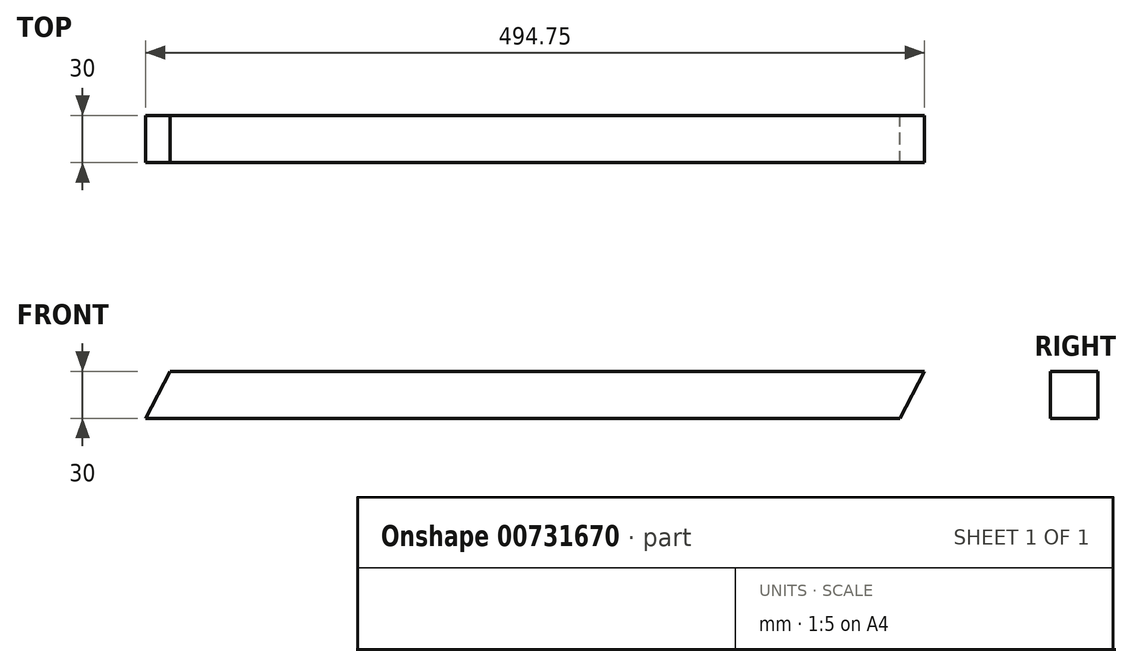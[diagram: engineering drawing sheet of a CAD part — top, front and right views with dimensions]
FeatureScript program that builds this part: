
annotation { "Feature Type Name" : "Feature", "Feature Type Description" : "" }
export const myFeature = defineFeature(function(context is Context, id is Id, definition is map)
    precondition{}
    {
        {
            var Q0;
            Q0=qCreatedBy(makeId("Front.planeOp"),FACE);
            var sketch = newSketch(context, id + "F0", { "sketchPlane" : qUnion([Q0])});
            skLineSegment(sketch, "E0", {"start": v(-108.8, 0) * mm, "end": v(370.34, 0) * mm});
            skLineSegment(sketch, "E1", {"start": v(-108.8, 0) * mm, "end": v(-93.18, 30) * mm});
            skLineSegment(sketch, "E2", {"start": v(-93.18, 30) * mm, "end": v(385.95, 30) * mm});
            skLineSegment(sketch, "E3", {"start": v(385.95, 30) * mm, "end": v(370.34, 0) * mm});
            skSolve(sketch);
        }
        {
            var Q0;
            Q0 = qSketchRegion(id + "F0", true);
            extrude(context, id + "F1", {"entities" : qUnion([Q0]), "depth" : 30 * mm, "offsetDistance" : 25 * mm});
        }
    });
